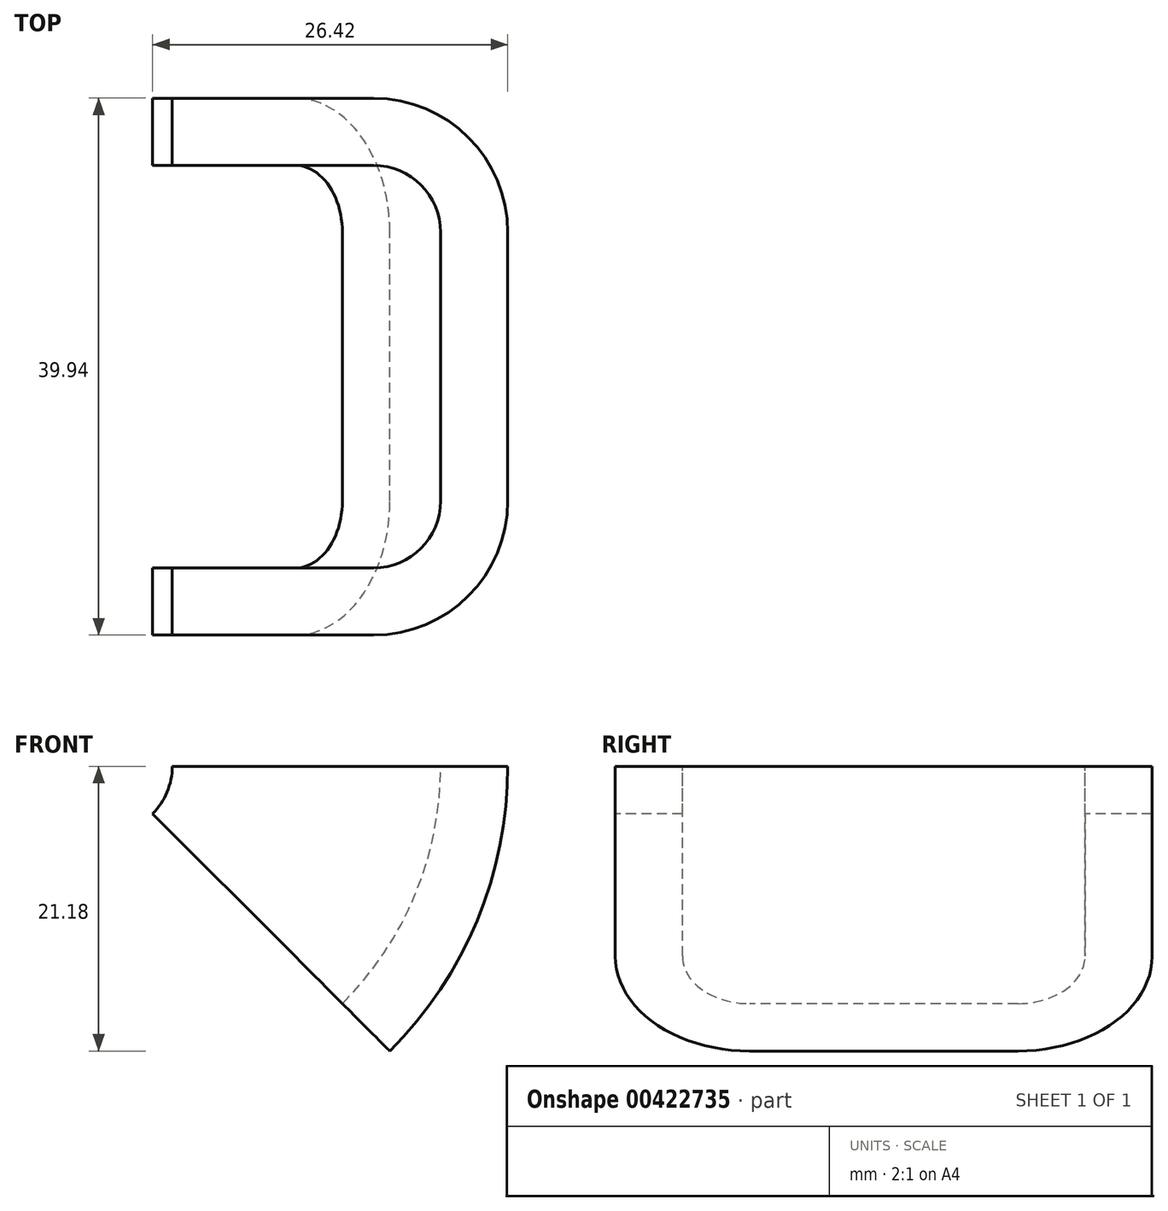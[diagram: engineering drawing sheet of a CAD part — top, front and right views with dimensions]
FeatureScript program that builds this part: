
annotation { "Feature Type Name" : "Feature", "Feature Type Description" : "" }
export const myFeature = defineFeature(function(context is Context, id is Id, definition is map)
    precondition{}
    {
        {
            var Q0;
            Q0=qCreatedBy(makeId("Top.planeOp"),FACE);
            var sketch = newSketch(context, id + "F0", { "sketchPlane" : qUnion([Q0])});
            skLineSegment(sketch, "E0.0", {"start": v(-198.26, -104.3) * mm, "end": v(-213.24, -104.3) * mm});
            skLineSegment(sketch, "E0.1", {"start": v(-198.26, -139.04) * mm, "end": v(-213.24, -139.04) * mm});
            skArc(sketch, "E0.2", {"start": v(-198.26, -139.04) * mm, "mid": v(-193.04, -136.88) * mm, "end": v(-190.87, -131.65) * mm});
            skLineSegment(sketch, "E0.3", {"start": v(-190.87, -111.69) * mm, "end": v(-190.87, -131.65) * mm});
            skArc(sketch, "E0.4", {"start": v(-190.87, -111.69) * mm, "mid": v(-193.04, -106.46) * mm, "end": v(-198.26, -104.3) * mm});
            skArc(sketch, "E1.0.0", {"start": v(-198.26, -136.65) * mm, "mid": v(-194.73, -135.18) * mm, "end": v(-193.27, -131.65) * mm});
            skLineSegment(sketch, "E1.0.1", {"start": v(-198.26, -136.65) * mm, "end": v(-213.24, -136.65) * mm});
            skLineSegment(sketch, "E1.0.2", {"start": v(-213.24, -136.65) * mm, "end": v(-213.24, -141.64) * mm});
            skLineSegment(sketch, "E1.0.3", {"start": v(-213.24, -141.64) * mm, "end": v(-198.26, -141.64) * mm});
            skArc(sketch, "E1.0.4", {"start": v(-198.26, -141.64) * mm, "mid": v(-191.2, -138.71) * mm, "end": v(-188.28, -131.65) * mm});
            skLineSegment(sketch, "E1.0.5", {"start": v(-188.28, -131.65) * mm, "end": v(-188.28, -111.69) * mm});
            skArc(sketch, "E1.0.6", {"start": v(-188.28, -111.69) * mm, "mid": v(-191.2, -104.63) * mm, "end": v(-198.26, -101.7) * mm});
            skLineSegment(sketch, "E1.0.7", {"start": v(-198.26, -101.7) * mm, "end": v(-213.24, -101.7) * mm});
            skLineSegment(sketch, "E1.0.8", {"start": v(-213.24, -101.7) * mm, "end": v(-213.24, -106.7) * mm});
            skLineSegment(sketch, "E1.0.9", {"start": v(-213.24, -106.7) * mm, "end": v(-198.26, -106.7) * mm});
            skArc(sketch, "E1.0.10", {"start": v(-193.27, -111.69) * mm, "mid": v(-194.73, -108.16) * mm, "end": v(-198.26, -106.7) * mm});
            skLineSegment(sketch, "E1.0.11", {"start": v(-193.27, -111.69) * mm, "end": v(-193.27, -131.65) * mm});
            skLineSegment(sketch, "E2", {"start": v(-218.24, -141.64) * mm, "end": v(-218.24, -101.7) * mm});
            skSolve(sketch);
        }
        {
            var Q0;
            {var subQ5=sQuery(id+"F0.wireOp",EDGE,"E0.0");Q0=makeQuery(id+"F0.imprint","IMPRINT",FACE,{"disambiguationData":[TD([[makeQuery(id+"F0.imprint","IMPRINT",EDGE,{"derivedFrom":subQ5}),1.0]])]});}
            var Q1;
            {var subQ3=sQuery(id+"F0.wireOp",EDGE,"E0.0");Q1=makeQuery(id+"F0.imprint","IMPRINT",FACE,{"disambiguationData":[TD([[makeQuery(id+"F0.imprint","IMPRINT",EDGE,{"derivedFrom":subQ3}),-1.0]])]});}
            var Q2;
            Q2=sQuery(id+"F0.wireOp",EDGE,"E2");
            revolve(context, id + "F1", {"entities" : qUnion([Q0, Q1]), "axis" : qUnion([Q2]), "revolveType" : RevolveType.ONE_DIRECTION, "angle" : 45 * degree});
        }
    });
